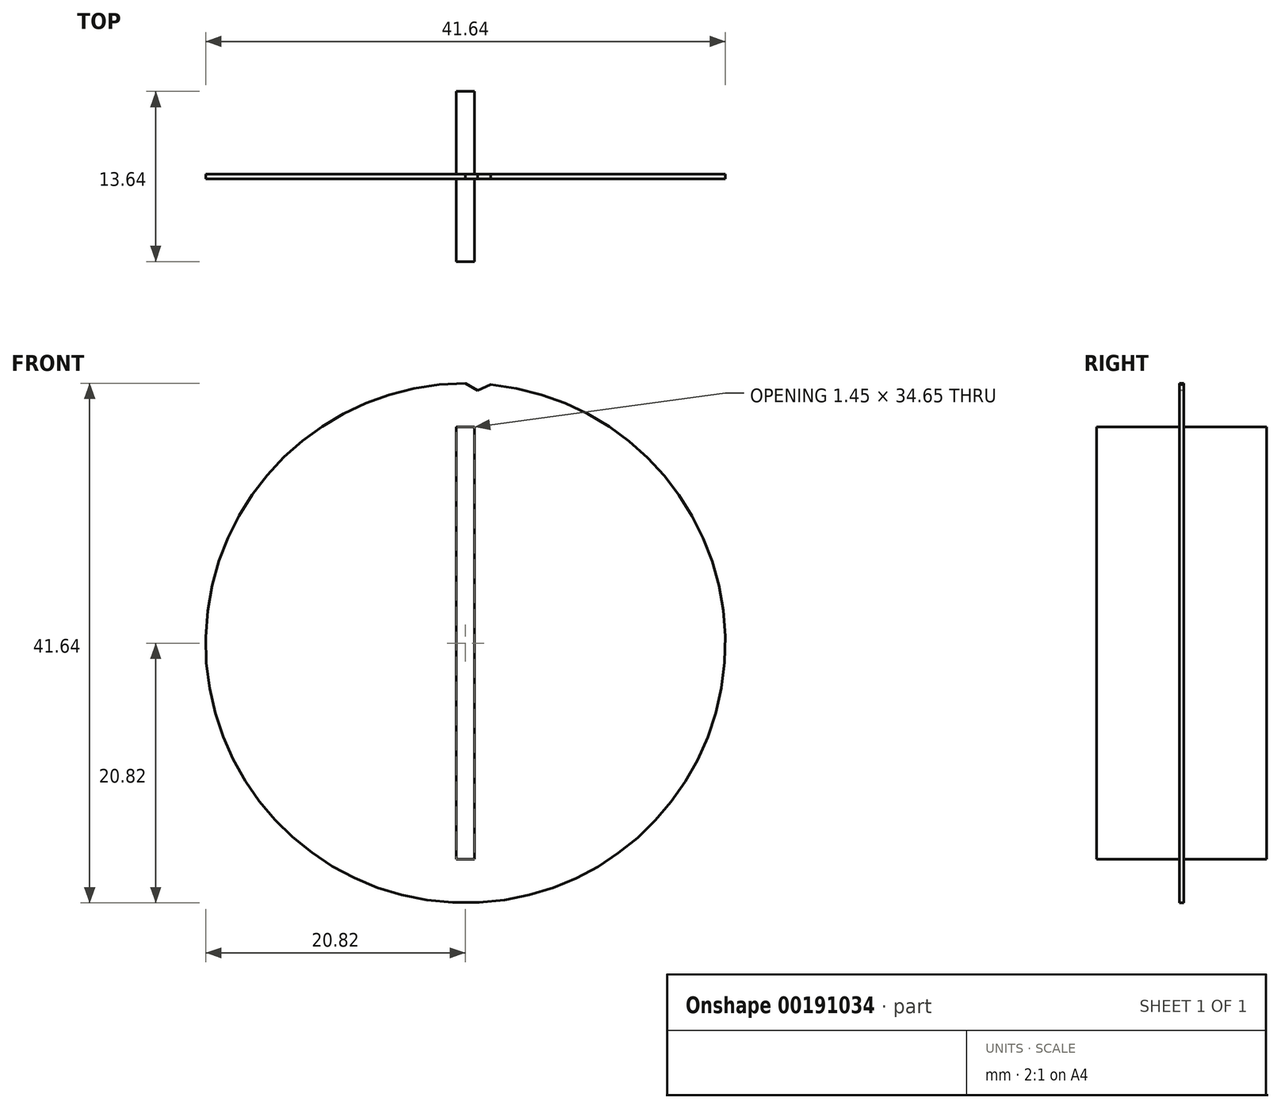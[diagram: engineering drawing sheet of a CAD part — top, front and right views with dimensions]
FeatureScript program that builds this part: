
annotation { "Feature Type Name" : "Feature", "Feature Type Description" : "" }
export const myFeature = defineFeature(function(context is Context, id is Id, definition is map)
    precondition{}
    {
        {
            var Q0;
            Q0=qCreatedBy(makeId("Front.planeOp"),FACE);
            var sketch = newSketch(context, id + "F0", { "sketchPlane" : qUnion([Q0])});
            skCircle(sketch, "E0", {"center": v(0, 0) * mm, "radius": 17.32 * mm});
            skSolve(sketch);
        }
        {
            var Q0;
            Q0=qCreatedBy(makeId("Front.planeOp"),FACE);
            var sketch = newSketch(context, id + "F1", { "sketchPlane" : qUnion([Q0])});
            skCircle(sketch, "E1", {"center": v(0, 0) * mm, "radius": 20.82 * mm});
            skSolve(sketch);
        }
        {
            var Q0;
            Q0=makeQuery(id+"F0.imprint","IMPRINT",FACE,{"disambiguationData":[TD([[makeQuery(id+"F0.imprint","IMPRINT",EDGE,{"derivedFrom":sQuery(id+"F0.wireOp",EDGE,"E0")}),1.0]])]});
            var Q1;
            Q1=makeQuery(id+"F1.imprint","IMPRINT",FACE,{"disambiguationData":[TD([[makeQuery(id+"F1.imprint","IMPRINT",EDGE,{"derivedFrom":sQuery(id+"F1.wireOp",EDGE,"E1")}),1.0]])]});
            extrude(context, id + "F2", {"entities" : qUnion([Q0, Q1]), "endBound" : BoundingType.SYMMETRIC, "depth" : 0.37 * mm});
        }
        {
            var Q0;
            Q0=makeQuery(id+"F2.opExtrude","CAP_FACE",FACE,{"disambiguationData":[OSD([sQuery(id+"F1.wireOp",EDGE,"E1")])],"isStart":false});
            var sketch = newSketch(context, id + "F3", { "sketchPlane" : qUnion([Q0])});
            skLineSegment(sketch, "E2", {"start": v(0, 20.82) * mm, "end": v(0.98, 20.26) * mm});
            skLineSegment(sketch, "E3", {"start": v(0.98, 20.26) * mm, "end": v(2.03, 20.72) * mm});
            skSolve(sketch);
        }
        {
            var Q0;
            {var subQ0=sQuery(id+"F3.wireOp",EDGE,"E2");Q0=makeQuery(id+"F3.imprint","IMPRINT",FACE,{"disambiguationData":[TD([[makeQuery(id+"F3.imprint","IMPRINT",EDGE,{"derivedFrom":subQ0}),1.0]])]});}
            extrude(context, id + "F4", {"entities" : qUnion([Q0]), "operationType" : NewBodyOperationType.REMOVE, "endBound" : BoundingType.THROUGH_ALL, "oppositeDirection" : true, "depth" : 25.4 * mm});
        }
        {
            var Q0;
            Q0=qCreatedBy(makeId("Right.planeOp"),FACE);
            var sketch = newSketch(context, id + "F5", { "sketchPlane" : qUnion([Q0])});
            skLineSegment(sketch, "E4", {"start": v(0, 0) * mm, "end": v(-3.9, 0) * mm, "construction": true});
            skSolve(sketch);
        }
        {
            var Q0;
            Q0=qCreatedBy(makeId("Front.planeOp"),FACE);
            var sketch = newSketch(context, id + "F6", { "sketchPlane" : qUnion([Q0])});
            skLineSegment(sketch, "E5.bottom", {"start": v(0.72, 17.32) * mm, "end": v(-0.72, 17.32) * mm});
            skLineSegment(sketch, "E5.top", {"start": v(0.72, -17.32) * mm, "end": v(-0.72, -17.32) * mm});
            skLineSegment(sketch, "E5.left", {"start": v(0.72, 17.32) * mm, "end": v(0.72, -17.32) * mm});
            skLineSegment(sketch, "E5.right", {"start": v(-0.72, 17.32) * mm, "end": v(-0.72, -17.32) * mm});
            skPoint(sketch, "E5.middle", {"position": v(0, 0) * mm});
            skSolve(sketch);
        }
        {
            var Q0;
            Q0 = qSketchRegion(id + "F6", true);
            extrude(context, id + "F7", {"entities" : qUnion([Q0]), "operationType" : NewBodyOperationType.ADD, "endBound" : BoundingType.SYMMETRIC, "depth" : 13.64 * mm});
        }
    });
